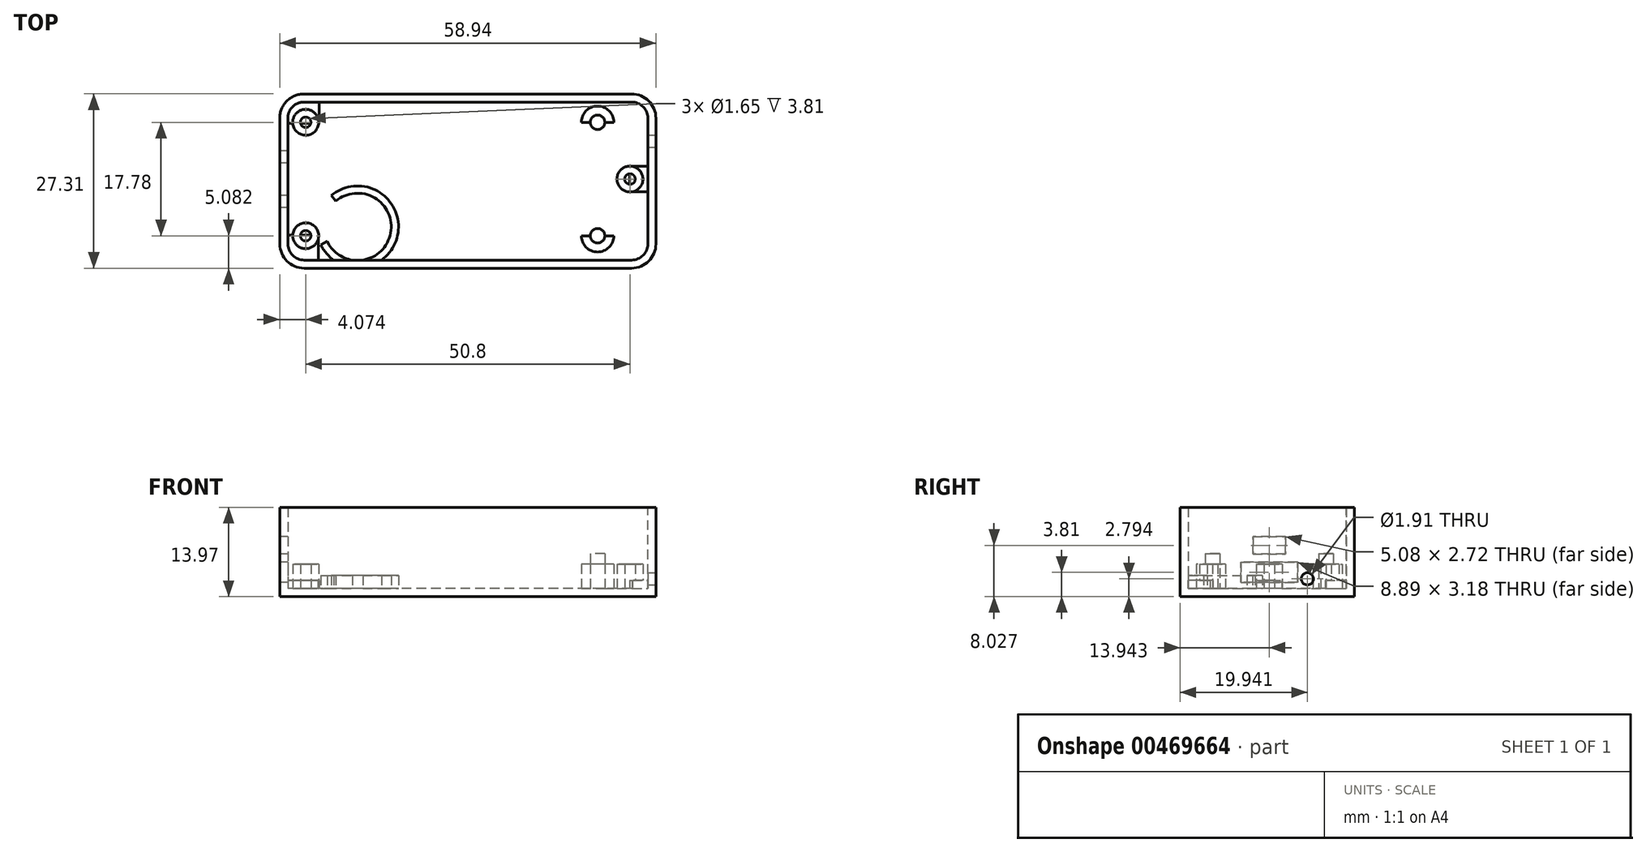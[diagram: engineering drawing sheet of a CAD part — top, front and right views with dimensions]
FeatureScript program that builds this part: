
annotation { "Feature Type Name" : "Feature", "Feature Type Description" : "" }
export const myFeature = defineFeature(function(context is Context, id is Id, definition is map)
    precondition{}
    {
        {
            var Q0;
            Q0=qCreatedBy(makeId("Top.planeOp"),FACE);
            var sketch = newSketch(context, id + "F0", { "sketchPlane" : qUnion([Q0])});
            skLineSegment(sketch, "E0.bottom", {"start": v(29.72, -13.97) * mm, "end": v(-21.58, -13.97) * mm});
            skLineSegment(sketch, "E0.top", {"start": v(29.72, 13.34) * mm, "end": v(-21.6, 13.34) * mm});
            skLineSegment(sketch, "E0.left", {"start": v(33.53, -10.16) * mm, "end": v(33.53, 9.53) * mm});
            skPoint(sketch, "E0.middle", {"position": v(1.52, 0) * mm});
            skLineSegment(sketch, "E1", {"start": v(-25.41, 9.52) * mm, "end": v(-25.39, -10.16) * mm});
            skPoint(sketch, "E2.visualSharp", {"position": v(-25.41, 13.34) * mm});
            skArc(sketch, "E2.filletArc", {"start": v(-21.6, 13.34) * mm, "mid": v(-24.3, 12.22) * mm, "end": v(-25.41, 9.52) * mm});
            skPoint(sketch, "E3.visualSharp", {"position": v(-25.38, -13.97) * mm});
            skArc(sketch, "E3.filletArc", {"start": v(-25.39, -10.16) * mm, "mid": v(-24.27, -12.85) * mm, "end": v(-21.58, -13.97) * mm});
            skPoint(sketch, "E4.visualSharp", {"position": v(33.53, 13.34) * mm});
            skArc(sketch, "E4.filletArc", {"start": v(33.53, 9.53) * mm, "mid": v(32.41, 12.22) * mm, "end": v(29.72, 13.34) * mm});
            skPoint(sketch, "E5.visualSharp", {"position": v(33.53, -13.97) * mm});
            skArc(sketch, "E5.filletArc", {"start": v(29.72, -13.97) * mm, "mid": v(32.41, -12.85) * mm, "end": v(33.53, -10.16) * mm});
            skSolve(sketch);
        }
        {
            var Q0;
            {var subQ0=sQuery(id+"F0.wireOp",EDGE,"E0.right");var subQ1=sQuery(id+"F0.wireOp",EDGE,"E0.top");var subQ2=makeQuery(id+"F0.imprint","INTERSECT",VERTEX,{"derivedFrom":[subQ1,subQ0]});Q0=makeQuery(id+"F0.imprint","IMPRINT",FACE,{"disambiguationData":[TD([[makeQuery(id+"F0.imprint","IMPRINT",EDGE,{"disambiguationData":[TD([[subQ2,1.0]])],"derivedFrom":subQ1}),1.0]])]});}
            var Q1;
            {var subQ0=sQuery(id+"F0.wireOp",EDGE,"E0.right");var subQ1=sQuery(id+"F0.wireOp",EDGE,"E0.bottom");var subQ2=makeQuery(id+"F0.imprint","INTERSECT",VERTEX,{"derivedFrom":[subQ1,subQ0]});Q1=makeQuery(id+"F0.imprint","IMPRINT",FACE,{"disambiguationData":[TD([[makeQuery(id+"F0.imprint","IMPRINT",EDGE,{"disambiguationData":[TD([[subQ2,1.0]])],"derivedFrom":subQ1}),-1.0]])]});}
            var Q2;
            {var subQ0=sQuery(id+"F0.wireOp",EDGE,"E0.left");var subQ1=sQuery(id+"F0.wireOp",EDGE,"E0.bottom");var subQ2=makeQuery(id+"F0.imprint","INTERSECT",VERTEX,{"derivedFrom":[subQ1,subQ0]});Q2=makeQuery(id+"F0.imprint","IMPRINT",FACE,{"disambiguationData":[TD([[makeQuery(id+"F0.imprint","IMPRINT",EDGE,{"disambiguationData":[TD([[subQ2,-1.0]])],"derivedFrom":subQ1}),-1.0]])]});}
            var Q3;
            {var subQ0=sQuery(id+"F0.wireOp",EDGE,"E0.left");var subQ1=sQuery(id+"F0.wireOp",EDGE,"E0.top");var subQ2=makeQuery(id+"F0.imprint","INTERSECT",VERTEX,{"derivedFrom":[subQ1,subQ0]});Q3=makeQuery(id+"F0.imprint","IMPRINT",FACE,{"disambiguationData":[TD([[makeQuery(id+"F0.imprint","IMPRINT",EDGE,{"disambiguationData":[TD([[subQ2,-1.0]])],"derivedFrom":subQ1}),1.0]])]});}
            var Q4;
            {var subQ0=sQuery(id+"F0.wireOp",EDGE,"77147c8d-bc3e-43fd-898d-79511b5ca3ae");var subQ1=makeQuery(id+"F0.imprint","INTERSECT",VERTEX,{"derivedFrom":[sQuery(id+"F0.wireOp",EDGE,"E0.bottom"),subQ0]});Q4=makeQuery(id+"F0.imprint","IMPRINT",FACE,{"disambiguationData":[TD([[makeQuery(id+"F0.imprint","IMPRINT",EDGE,{"disambiguationData":[TD([[subQ1,1.0]])],"derivedFrom":subQ0}),1.0]])]});}
            var Q5;
            {var subQ0=sQuery(id+"F0.wireOp",EDGE,"7fac53bc-fe44-4dcf-aa1a-77a17067d2a3");var subQ1=makeQuery(id+"F0.imprint","INTERSECT",VERTEX,{"derivedFrom":[sQuery(id+"F0.wireOp",EDGE,"E0.top"),subQ0]});Q5=makeQuery(id+"F0.imprint","IMPRINT",FACE,{"disambiguationData":[TD([[makeQuery(id+"F0.imprint","IMPRINT",EDGE,{"disambiguationData":[TD([[subQ1,1.0]])],"derivedFrom":subQ0}),1.0]])]});}
            var Q6;
            {var subQ0=sQuery(id+"F0.wireOp",EDGE,"jG86MAPj-qCsZ-eWPK-wZvu-NG4jCO74JAhP");var subQ1=makeQuery(id+"F0.imprint","INTERSECT",VERTEX,{"derivedFrom":[sQuery(id+"F0.wireOp",EDGE,"E0.top"),subQ0]});Q6=makeQuery(id+"F0.imprint","IMPRINT",FACE,{"disambiguationData":[TD([[makeQuery(id+"F0.imprint","IMPRINT",EDGE,{"disambiguationData":[TD([[subQ1,-1.0]])],"derivedFrom":subQ0}),1.0]])]});}
            var Q7;
            {var subQ0=sQuery(id+"F0.wireOp",EDGE,"jG86MAPj-qCsZ-eWPK-wZvu-NG4jCO74JAhP");Q7=makeQuery(id+"F0.imprint","IMPRINT",FACE,{"disambiguationData":[TD([[makeQuery(id+"F0.imprint","IMPRINT",EDGE,{"derivedFrom":subQ0}),-1.0]])]});}
            extrude(context, id + "F1", {"entities" : qUnion([Q0, Q1, Q2, Q3, Q4, Q5, Q6, Q7]), "offsetDistance" : 25.4 * mm, "depth" : 13.97 * mm});
        }
        {
            var Q0;
            Q0=makeQuery(id+"F1.opExtrude","CAP_FACE",FACE,{"disambiguationData":[OSD([sQuery(id+"F0.wireOp",EDGE,"E0.bottom"),sQuery(id+"F0.wireOp",EDGE,"E0.top"),sQuery(id+"F0.wireOp",EDGE,"E0.left"),sQuery(id+"F0.wireOp",EDGE,"E0.right")])],"isStart":false});
            shell(context, id + "F2", {"entities" : qUnion([Q0]), "thickness" : 1.27 * mm});
        }
        {
            var Q0;
            Q0=makeQuery(id+"F2.opShell","OFFSET_FACE",FACE,{"disambiguationData":[OSD([sQuery(id+"F0.wireOp",EDGE,"E0.bottom"),sQuery(id+"F0.wireOp",EDGE,"E0.top"),sQuery(id+"F0.wireOp",EDGE,"E0.left"),sQuery(id+"F0.wireOp",EDGE,"E0.right")])]});
            var sketch = newSketch(context, id + "F3", { "sketchPlane" : qUnion([Q0])});
            skCircle(sketch, "E6", {"center": v(-21.34, 8.9) * mm, "radius": 2.03 * mm});
            skCircle(sketch, "E7", {"center": v(24.38, 8.9) * mm, "radius": 1.14 * mm});
            skCircle(sketch, "E8", {"center": v(-21.34, -8.89) * mm, "radius": 2.03 * mm});
            skCircle(sketch, "E9", {"center": v(24.38, -8.89) * mm, "radius": 1.14 * mm});
            skLineSegment(sketch, "E10", {"start": v(24.38, -8.89) * mm, "end": v(26.92, -8.89) * mm});
            skLineSegment(sketch, "E11", {"start": v(26.92, 8.9) * mm, "end": v(24.38, 8.9) * mm});
            skCircle(sketch, "E12", {"center": v(-21.34, 8.9) * mm, "radius": 0.83 * mm});
            skCircle(sketch, "E13", {"center": v(-21.34, -8.89) * mm, "radius": 0.83 * mm});
            skLineSegment(sketch, "E14", {"start": v(24.38, 8.9) * mm, "end": v(21.84, 8.9) * mm});
            skLineSegment(sketch, "E15", {"start": v(24.38, -8.89) * mm, "end": v(21.84, -8.89) * mm});
            skArc(sketch, "E16", {"start": v(21.84, -8.89) * mm, "mid": v(24.38, -11.43) * mm, "end": v(26.92, -8.89) * mm});
            skArc(sketch, "E17", {"start": v(26.92, 8.9) * mm, "mid": v(24.38, 11.43) * mm, "end": v(21.84, 8.9) * mm});
            skSolve(sketch);
        }
        {
            var Q0;
            Q0=makeQuery(id+"F3.imprint","IMPRINT",FACE,{"disambiguationData":[TD([[makeQuery(id+"F3.imprint","IMPRINT",EDGE,{"derivedFrom":sQuery(id+"F3.wireOp",EDGE,"E6")}),1.0]])]});
            var Q1;
            Q1=makeQuery(id+"F3.imprint","IMPRINT",FACE,{"disambiguationData":[TD([[makeQuery(id+"F3.imprint","IMPRINT",EDGE,{"derivedFrom":sQuery(id+"F3.wireOp",EDGE,"E8")}),1.0]])]});
            var Q2;
            {var subQ5=sQuery(id+"F3.wireOp",EDGE,"E16");Q2=makeQuery(id+"F3.imprint","IMPRINT",FACE,{"disambiguationData":[TD([[makeQuery(id+"F3.imprint","IMPRINT",EDGE,{"derivedFrom":subQ5}),1.0]])]});}
            var Q3;
            {var subQ5=sQuery(id+"F3.wireOp",EDGE,"E17");Q3=makeQuery(id+"F3.imprint","IMPRINT",FACE,{"disambiguationData":[TD([[makeQuery(id+"F3.imprint","IMPRINT",EDGE,{"derivedFrom":subQ5}),1.0]])]});}
            var Q4;
            Q4=sQuery(id+"F3.wireOp",EDGE,"E6");
            var Q5;
            Q5=sQuery(id+"F3.wireOp",EDGE,"E8");
            extrude(context, id + "F4", {"entities" : qUnion([Q0, Q1, Q2, Q3]), "operationType" : NewBodyOperationType.ADD, "surfaceEntities" : qUnion([Q4, Q5]), "depth" : 3.8 * mm});
        }
        {
            var Q0;
            Q0=makeQuery(id+"F3.imprint","IMPRINT",FACE,{"disambiguationData":[TD([[makeQuery(id+"F3.imprint","IMPRINT",EDGE,{"derivedFrom":sQuery(id+"F3.wireOp",EDGE,"E7")}),1.0]])]});
            var Q1;
            Q1=makeQuery(id+"F3.imprint","IMPRINT",FACE,{"disambiguationData":[TD([[makeQuery(id+"F3.imprint","IMPRINT",EDGE,{"derivedFrom":sQuery(id+"F3.wireOp",EDGE,"E9")}),1.0]])]});
            var Q2;
            Q2=sQuery(id+"F3.wireOp",EDGE,"E7");
            var Q3;
            Q3=sQuery(id+"F3.wireOp",EDGE,"E9");
            extrude(context, id + "F5", {"entities" : qUnion([Q0, Q1]), "operationType" : NewBodyOperationType.ADD, "surfaceEntities" : qUnion([Q2, Q3]), "depth" : 5.46 * mm});
        }
        {
            var Q0;
            Q0=makeQuery(id+"F3.imprint","IMPRINT",FACE,{"disambiguationData":[TD([[makeQuery(id+"F3.imprint","IMPRINT",EDGE,{"derivedFrom":sQuery(id+"F3.wireOp",EDGE,"E12")}),1.0]])]});
            var Q1;
            Q1=makeQuery(id+"F3.imprint","IMPRINT",FACE,{"disambiguationData":[TD([[makeQuery(id+"F3.imprint","IMPRINT",EDGE,{"derivedFrom":sQuery(id+"F3.wireOp",EDGE,"E13")}),1.0]])]});
            var Q2;
            Q2=sQuery(id+"F3.wireOp",EDGE,"E12");
            var Q3;
            Q3=sQuery(id+"F3.wireOp",EDGE,"E13");
            extrude(context, id + "F6", {"entities" : qUnion([Q0, Q1]), "operationType" : NewBodyOperationType.REMOVE, "surfaceEntities" : qUnion([Q2, Q3]), "depth" : 2.54 * mm});
        }
        {
            var Q0;
            Q0=makeQuery(id+"F1.opExtrude","SWEPT_FACE",FACE,{"disambiguationData":[OSD([sQuery(id+"F0.wireOp",EDGE,"E1")])]});
            var sketch = newSketch(context, id + "F7", { "sketchPlane" : qUnion([Q0])});
            skLineSegment(sketch, "E18.bottom", {"start": v(-4.45, 2.22) * mm, "end": v(4.45, 2.22) * mm});
            skLineSegment(sketch, "E18.top", {"start": v(-4.45, 5.4) * mm, "end": v(4.45, 5.4) * mm});
            skLineSegment(sketch, "E18.left", {"start": v(-4.45, 2.22) * mm, "end": v(-4.45, 5.4) * mm});
            skLineSegment(sketch, "E18.right", {"start": v(4.45, 2.22) * mm, "end": v(4.45, 5.4) * mm});
            skPoint(sketch, "E18.middle", {"position": v(0, 3.81) * mm});
            skLineSegment(sketch, "E19.bottom", {"start": v(2.54, 6.67) * mm, "end": v(-2.54, 6.67) * mm});
            skLineSegment(sketch, "E19.top", {"start": v(2.54, 9.39) * mm, "end": v(-2.54, 9.39) * mm});
            skLineSegment(sketch, "E19.left", {"start": v(2.54, 6.67) * mm, "end": v(2.54, 9.39) * mm});
            skLineSegment(sketch, "E19.right", {"start": v(-2.54, 6.67) * mm, "end": v(-2.54, 9.39) * mm});
            skPoint(sketch, "E19.middle", {"position": v(0, 8.03) * mm});
            skSolve(sketch);
        }
        {
            var Q0;
            Q0 = qSketchRegion(id + "F7", true);
            extrude(context, id + "F8", {"entities" : qUnion([Q0]), "operationType" : NewBodyOperationType.REMOVE, "oppositeDirection" : true, "depth" : 1.9 * mm});
        }
        {
            var Q0;
            Q0=makeQuery(id+"F1.opExtrude","SWEPT_FACE",FACE,{"disambiguationData":[OSD([sQuery(id+"F0.wireOp",EDGE,"E0.left")])]});
            var sketch = newSketch(context, id + "F9", { "sketchPlane" : qUnion([Q0])});
            skCircle(sketch, "E20", {"center": v(5.97, 2.8) * mm, "radius": 0.95 * mm});
            skSolve(sketch);
        }
        {
            var Q0;
            Q0=makeQuery(id+"F9.imprint","IMPRINT",FACE,{"disambiguationData":[TD([[makeQuery(id+"F9.imprint","IMPRINT",EDGE,{"derivedFrom":sQuery(id+"F9.wireOp",EDGE,"E20")}),1.0]])]});
            var Q1;
            Q1=sQuery(id+"F9.wireOp",EDGE,"E20");
            extrude(context, id + "F10", {"entities" : qUnion([Q0]), "operationType" : NewBodyOperationType.REMOVE, "surfaceEntities" : qUnion([Q1]), "oppositeDirection" : true, "depth" : 1.9 * mm});
        }
        {
            var Q0;
            Q0=makeQuery(id+"F3.imprint","IMPRINT",FACE,{"disambiguationData":[TD([[makeQuery(id+"F3.imprint","IMPRINT",EDGE,{"derivedFrom":sQuery(id+"F3.wireOp",EDGE,"E6")}),-1.0]])]});
            var sketch = newSketch(context, id + "F11", { "sketchPlane" : qUnion([Q0])});
            skCircle(sketch, "E21", {"center": v(29.46, 0) * mm, "radius": 2.03 * mm});
            skCircle(sketch, "E22", {"center": v(29.46, 0) * mm, "radius": 0.83 * mm});
            skSolve(sketch);
        }
        {
            var Q0;
            Q0 = qSketchRegion(id + "F11", true);
            var Q1;
            Q1=makeQuery(id+"F11.imprint","IMPRINT",FACE,{"disambiguationData":[TD([[makeQuery(id+"F11.imprint","IMPRINT",EDGE,{"derivedFrom":sQuery(id+"F11.wireOp",EDGE,"E21")}),1.0]])]});
            extrude(context, id + "F12", {"entities" : qUnion([Q0, Q1]), "operationType" : NewBodyOperationType.ADD, "depth" : 3.8 * mm});
        }
        {
            var Q0;
            Q0=makeQuery(id+"F3.imprint","IMPRINT",FACE,{"disambiguationData":[TD([[makeQuery(id+"F3.imprint","IMPRINT",EDGE,{"derivedFrom":sQuery(id+"F3.wireOp",EDGE,"E6")}),-1.0]])]});
            var sketch = newSketch(context, id + "F13", { "sketchPlane" : qUnion([Q0])});
            skArc(sketch, "E23", {"start": v(-17.98, -9.72) * mm, "mid": v(-8.06, -8.62) * mm, "end": v(-16.6, -3.46) * mm});
            skArc(sketch, "E24", {"start": v(-18.97, -10.31) * mm, "mid": v(-6.93, -8.82) * mm, "end": v(-17.33, -2.58) * mm});
            skLineSegment(sketch, "E25", {"start": v(-18.97, -10.31) * mm, "end": v(-17.98, -9.72) * mm});
            skLineSegment(sketch, "E26", {"start": v(-17.33, -2.58) * mm, "end": v(-16.6, -3.46) * mm});
            skSolve(sketch);
        }
        {
            var Q0;
            Q0=makeQuery(id+"F13.imprint","IMPRINT",FACE,{"disambiguationData":[TD([[makeQuery(id+"F13.imprint","IMPRINT",EDGE,{"derivedFrom":sQuery(id+"F13.wireOp",EDGE,"E23")}),-1.0]])]});
            extrude(context, id + "F14", {"entities" : qUnion([Q0]), "operationType" : NewBodyOperationType.ADD, "depth" : 2.03 * mm});
        }
        {
            var Q0;
            Q0=makeQuery(id+"F3.imprint","IMPRINT",FACE,{"disambiguationData":[TD([[makeQuery(id+"F3.imprint","IMPRINT",EDGE,{"derivedFrom":sQuery(id+"F3.wireOp",EDGE,"E6")}),-1.0]])]});
            var sketch = newSketch(context, id + "F15", { "sketchPlane" : qUnion([Q0])});
            skLineSegment(sketch, "E27.bottom", {"start": v(29.44, 2) * mm, "end": v(32.75, 2) * mm});
            skLineSegment(sketch, "E27.top", {"start": v(29.44, -2) * mm, "end": v(32.75, -2) * mm});
            skLineSegment(sketch, "E27.left", {"start": v(29.44, 2) * mm, "end": v(29.44, -2) * mm});
            skLineSegment(sketch, "E27.right", {"start": v(32.75, 2) * mm, "end": v(32.75, -2) * mm});
            skLineSegment(sketch, "E28.bottom", {"start": v(-19.25, 8.76) * mm, "end": v(-24.25, 8.76) * mm});
            skLineSegment(sketch, "E28.top", {"start": v(-19.25, 12.19) * mm, "end": v(-24.25, 12.19) * mm});
            skLineSegment(sketch, "E28.left", {"start": v(-19.25, 8.76) * mm, "end": v(-19.25, 12.19) * mm});
            skLineSegment(sketch, "E28.right", {"start": v(-24.25, 8.76) * mm, "end": v(-24.25, 12.19) * mm});
            skLineSegment(sketch, "E29.bottom", {"start": v(-19.35, -8.81) * mm, "end": v(-24.25, -8.81) * mm});
            skLineSegment(sketch, "E29.top", {"start": v(-19.35, -12.83) * mm, "end": v(-24.25, -12.83) * mm});
            skLineSegment(sketch, "E29.left", {"start": v(-19.35, -8.81) * mm, "end": v(-19.35, -12.83) * mm});
            skLineSegment(sketch, "E29.right", {"start": v(-24.25, -8.81) * mm, "end": v(-24.25, -12.83) * mm});
            skSolve(sketch);
        }
        {
            var Q0;
            Q0 = qSketchRegion(id + "F15", true);
            extrude(context, id + "F16", {"entities" : qUnion([Q0]), "operationType" : NewBodyOperationType.ADD, "depth" : 1.27 * mm});
        }
    });
